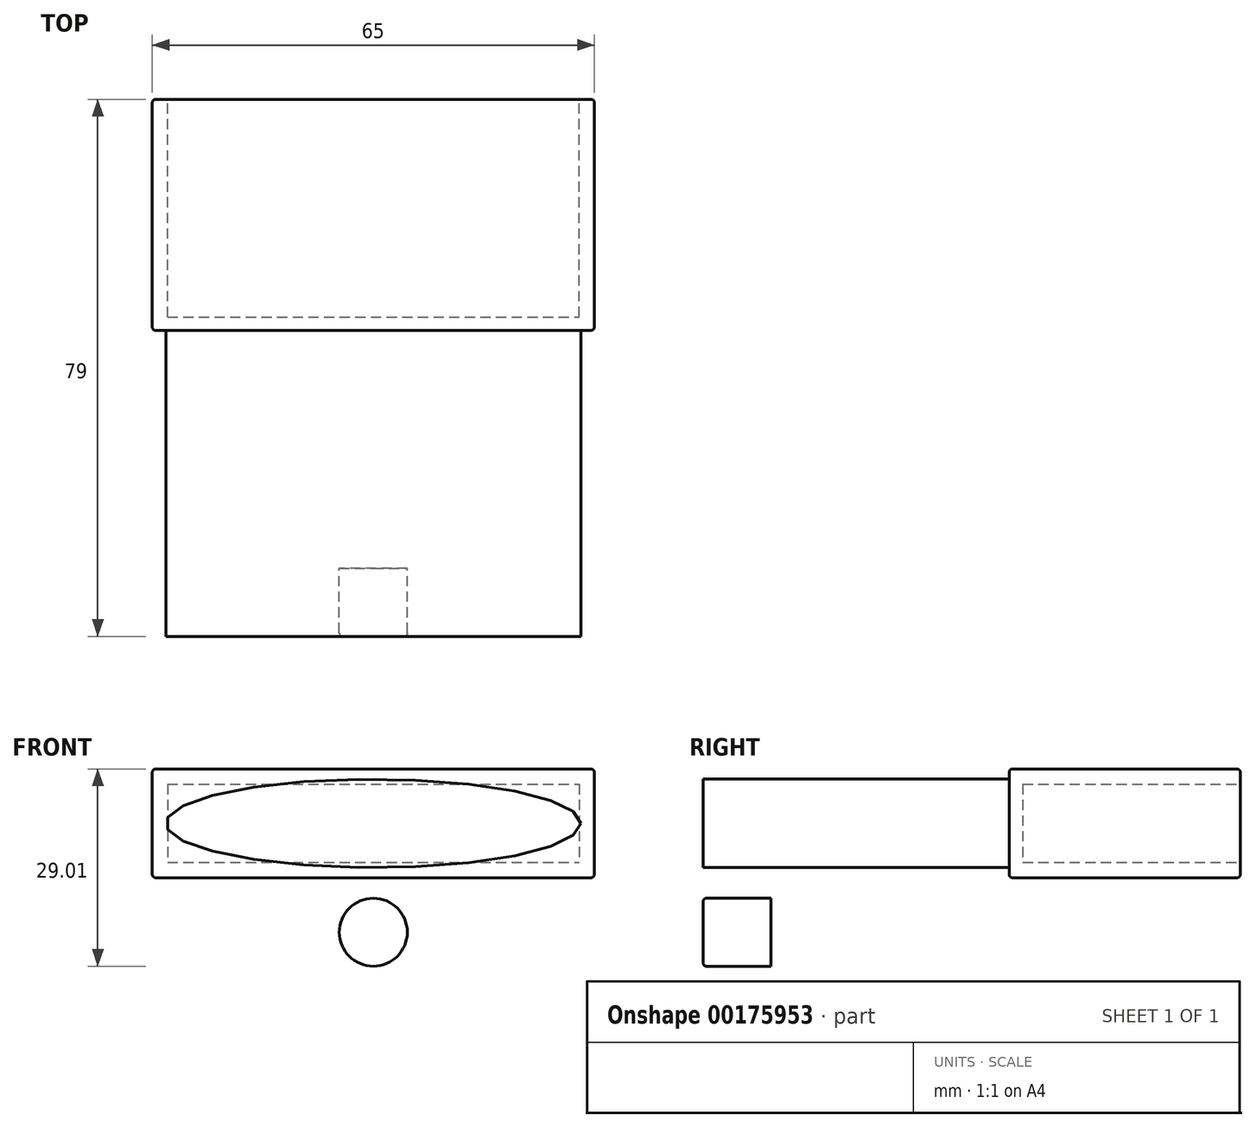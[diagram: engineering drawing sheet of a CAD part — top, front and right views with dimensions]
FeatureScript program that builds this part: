
annotation { "Feature Type Name" : "Feature", "Feature Type Description" : "" }
export const myFeature = defineFeature(function(context is Context, id is Id, definition is map)
    precondition{}
    {
        {
            var Q0;
            Q0=qCreatedBy(makeId("Front.planeOp"),FACE);
            var sketch = newSketch(context, id + "F0", { "sketchPlane" : qUnion([Q0])});
            skPoint(sketch, "E0.middle", {"position": v(0, 0) * mm});
            skLineSegment(sketch, "E1.bottom", {"start": v(32.5, 8) * mm, "end": v(-32.5, 8) * mm});
            skLineSegment(sketch, "E1.top", {"start": v(32.5, -8) * mm, "end": v(-32.5, -8) * mm});
            skLineSegment(sketch, "E1.left", {"start": v(32.5, 8) * mm, "end": v(32.5, -8) * mm});
            skLineSegment(sketch, "E1.right", {"start": v(-32.5, 8) * mm, "end": v(-32.5, -8) * mm});
            skSolve(sketch);
        }
        {
            var Q0;
            Q0=makeQuery(id+"F0.imprint","IMPRINT",FACE,{"disambiguationData":[TD([[makeQuery(id+"F0.imprint","IMPRINT",EDGE,{"derivedFrom":sQuery(id+"F0.wireOp",EDGE,"E1.bottom")}),1.0]])]});
            extrude(context, id + "F1", {"entities" : qUnion([Q0]), "depth" : 34 * mm});
        }
        {
            var Q0;
            Q0=makeQuery(id+"F1.opExtrude","CAP_FACE",FACE,{"disambiguationData":[OSD([sQuery(id+"F0.wireOp",EDGE,"E1.bottom"),sQuery(id+"F0.wireOp",EDGE,"E1.top"),sQuery(id+"F0.wireOp",EDGE,"E1.left"),sQuery(id+"F0.wireOp",EDGE,"E1.right")])],"isStart":false});
            var sketch = newSketch(context, id + "F2", { "sketchPlane" : qUnion([Q0])});
            skEllipse(sketch, "E2", {"center": v(0, 0) * mm, "majorRadius": 30.5 * mm, "minorRadius": 6.5 * mm, "majorAxis": v(1, 0)});
            skSolve(sketch);
        }
        {
            var Q0;
            Q0=makeQuery(id+"F1.opExtrude","CAP_FACE",FACE,{"disambiguationData":[OSD([sQuery(id+"F0.wireOp",EDGE,"E1.bottom"),sQuery(id+"F0.wireOp",EDGE,"E1.top"),sQuery(id+"F0.wireOp",EDGE,"E1.left"),sQuery(id+"F0.wireOp",EDGE,"E1.right")])],"isStart":true});
            var sketch = newSketch(context, id + "F3", { "sketchPlane" : qUnion([Q0])});
            skLineSegment(sketch, "E3.bottom", {"start": v(30.25, 5.75) * mm, "end": v(-30.25, 5.75) * mm});
            skLineSegment(sketch, "E3.top", {"start": v(30.25, -5.75) * mm, "end": v(-30.25, -5.75) * mm});
            skLineSegment(sketch, "E3.left", {"start": v(30.25, 5.75) * mm, "end": v(30.25, -5.75) * mm});
            skLineSegment(sketch, "E3.right", {"start": v(-30.25, 5.75) * mm, "end": v(-30.25, -5.75) * mm});
            skPoint(sketch, "E3.middle", {"position": v(0, 0) * mm});
            skSolve(sketch);
        }
        {
            var Q0;
            Q0=makeQuery(id+"F3.imprint","IMPRINT",FACE,{"disambiguationData":[TD([[makeQuery(id+"F3.imprint","IMPRINT",EDGE,{"derivedFrom":sQuery(id+"F3.wireOp",EDGE,"E3.bottom")}),1.0]])]});
            extrude(context, id + "F4", {"entities" : qUnion([Q0]), "operationType" : NewBodyOperationType.REMOVE, "oppositeDirection" : true, "depth" : 32 * mm});
        }
        {
            var Q0;
            Q0=makeQuery(id+"F2.imprint","IMPRINT",FACE,{"disambiguationData":[TD([[makeQuery(id+"F2.imprint","IMPRINT",EDGE,{"derivedFrom":sQuery(id+"F2.wireOp",EDGE,"E2")}),1.0]])]});
            extrude(context, id + "F5", {"entities" : qUnion([Q0]), "operationType" : NewBodyOperationType.ADD, "depth" : 35 * mm});
        }
        {
            var Q0;
            Q0=makeQuery(id+"F5.opExtrude","CAP_FACE",FACE,{"disambiguationData":[OSD([sQuery(id+"F2.wireOp",EDGE,"E2")])],"isStart":false});
            var sketch = newSketch(context, id + "F6", { "sketchPlane" : qUnion([Q0])});
            skEllipse(sketch, "E4", {"center": v(0, 0) * mm, "majorRadius": 50.5 * mm, "minorRadius": 25.5 * mm, "majorAxis": v(1, -0.06)});
            skSolve(sketch);
        }
        {
            var Q0;
            Q0=makeQuery(id+"F6.imprint","IMPRINT",FACE,{"disambiguationData":[TD([[makeQuery(id+"F6.imprint","IMPRINT",EDGE,{"derivedFrom":makeQuery(id+"F5.opExtrude","CAP_EDGE",EDGE,{"disambiguationData":[OSD([sQuery(id+"F2.wireOp",EDGE,"E2")])],"isStart":false})}),1.0]])]});
            var Q1;
            Q1=makeQuery(id+"F6.imprint","IMPRINT",FACE,{"disambiguationData":[TD([[makeQuery(id+"F6.imprint","IMPRINT",EDGE,{"derivedFrom":sQuery(id+"F6.wireOp",EDGE,"E4")}),1.0]])]});
            extrude(context, id + "F7", {"entities" : qUnion([Q0, Q1]), "operationType" : NewBodyOperationType.ADD, "depth" : 10 * mm});
        }
        {
            var Q0;
            Q0=makeQuery(id+"F7.opExtrude","CAP_FACE",FACE,{"disambiguationData":[OSD([sQuery(id+"F6.wireOp",EDGE,"E4")])],"isStart":true});
            var sketch = newSketch(context, id + "F8", { "sketchPlane" : qUnion([Q0])});
            skCircle(sketch, "E5", {"center": v(40.39, 0) * mm, "radius": 5 * mm});
            skCircle(sketch, "E6", {"center": v(-40.39, 0) * mm, "radius": 5 * mm});
            skCircle(sketch, "E7", {"center": v(0, 16.01) * mm, "radius": 5 * mm});
            skCircle(sketch, "E8.MirrorC", {"center": v(0, -16.01) * mm, "radius": 5 * mm});
            skSolve(sketch);
        }
        {
            var Q0;
            Q0=makeQuery(id+"F8.imprint","IMPRINT",FACE,{"disambiguationData":[TD([[makeQuery(id+"F8.imprint","IMPRINT",EDGE,{"derivedFrom":sQuery(id+"F8.wireOp",EDGE,"E5")}),1.0]])]});
            var Q1;
            Q1=makeQuery(id+"F8.imprint","IMPRINT",FACE,{"disambiguationData":[TD([[makeQuery(id+"F8.imprint","IMPRINT",EDGE,{"derivedFrom":sQuery(id+"F8.wireOp",EDGE,"E7")}),1.0]])]});
            var Q2;
            Q2=makeQuery(id+"F8.imprint","IMPRINT",FACE,{"disambiguationData":[TD([[makeQuery(id+"F8.imprint","IMPRINT",EDGE,{"derivedFrom":sQuery(id+"F8.wireOp",EDGE,"E6")}),1.0]])]});
            var Q3;
            Q3=makeQuery(id+"F8.imprint","IMPRINT",FACE,{"disambiguationData":[TD([[makeQuery(id+"F8.imprint","IMPRINT",EDGE,{"derivedFrom":sQuery(id+"F8.wireOp",EDGE,"E8.MirrorC")}),-1.0]])]});
            extrude(context, id + "F9", {"entities" : qUnion([Q0, Q1, Q2, Q3]), "operationType" : NewBodyOperationType.REMOVE, "endBound" : BoundingType.THROUGH_ALL, "oppositeDirection" : true, "depth" : 25 * mm});
        }
        {
            var Q0;
            Q0=makeQuery(id+"F1.opExtrude","CAP_EDGE",EDGE,{"disambiguationData":[OSD([sQuery(id+"F0.wireOp",EDGE,"E1.bottom")])],"isStart":true});
            var Q1;
            Q1=makeQuery(id+"F4.boolean.opBoolean","COPY",EDGE,{"derivedFrom":makeQuery(id+"F4.opExtrude","CAP_EDGE",EDGE,{"disambiguationData":[OSD([sQuery(id+"F3.wireOp",EDGE,"E3.bottom")])],"isStart":true})});
            var Q2;
            Q2=makeQuery(id+"F4.boolean.opBoolean","COPY",EDGE,{"derivedFrom":makeQuery(id+"F4.opExtrude","CAP_EDGE",EDGE,{"disambiguationData":[OSD([sQuery(id+"F3.wireOp",EDGE,"E3.right")])],"isStart":true})});
            var Q3;
            Q3=makeQuery(id+"F4.boolean.opBoolean","COPY",EDGE,{"derivedFrom":makeQuery(id+"F4.opExtrude","CAP_EDGE",EDGE,{"disambiguationData":[OSD([sQuery(id+"F3.wireOp",EDGE,"E3.top")])],"isStart":true})});
            var Q4;
            Q4=makeQuery(id+"F1.opExtrude","CAP_EDGE",EDGE,{"disambiguationData":[OSD([sQuery(id+"F0.wireOp",EDGE,"E1.left")])],"isStart":true});
            var Q5;
            Q5=makeQuery(id+"F1.opExtrude","CAP_EDGE",EDGE,{"disambiguationData":[OSD([sQuery(id+"F0.wireOp",EDGE,"E1.top")])],"isStart":true});
            var Q6;
            Q6=makeQuery(id+"F1.opExtrude","CAP_EDGE",EDGE,{"disambiguationData":[OSD([sQuery(id+"F0.wireOp",EDGE,"E1.right")])],"isStart":true});
            var Q7;
            Q7=makeQuery(id+"F4.boolean.opBoolean","COPY",EDGE,{"derivedFrom":makeQuery(id+"F4.opExtrude","CAP_EDGE",EDGE,{"disambiguationData":[OSD([sQuery(id+"F3.wireOp",EDGE,"E3.left")])],"isStart":true})});
            var Q8;
            Q8=makeQuery(id+"F1.opExtrude","SWEPT_EDGE",EDGE,{"disambiguationData":[OSD([sQuery(id+"F0.wireOp",EDGE,"E1.bottom"),sQuery(id+"F0.wireOp",EDGE,"E1.right")])]});
            var Q9;
            Q9=makeQuery(id+"F1.opExtrude","SWEPT_EDGE",EDGE,{"disambiguationData":[OSD([sQuery(id+"F0.wireOp",EDGE,"E1.top"),sQuery(id+"F0.wireOp",EDGE,"E1.right")])]});
            var Q10;
            Q10=makeQuery(id+"F1.opExtrude","CAP_EDGE",EDGE,{"disambiguationData":[OSD([sQuery(id+"F0.wireOp",EDGE,"E1.right")])],"isStart":false});
            var Q11;
            Q11=makeQuery(id+"F1.opExtrude","CAP_EDGE",EDGE,{"disambiguationData":[OSD([sQuery(id+"F0.wireOp",EDGE,"E1.bottom")])],"isStart":false});
            var Q12;
            Q12=makeQuery(id+"F1.opExtrude","SWEPT_EDGE",EDGE,{"disambiguationData":[OSD([sQuery(id+"F0.wireOp",EDGE,"E1.bottom"),sQuery(id+"F0.wireOp",EDGE,"E1.left")])]});
            var Q13;
            Q13=makeQuery(id+"F1.opExtrude","SWEPT_EDGE",EDGE,{"disambiguationData":[OSD([sQuery(id+"F0.wireOp",EDGE,"E1.top"),sQuery(id+"F0.wireOp",EDGE,"E1.left")])]});
            var Q14;
            Q14=makeQuery(id+"F1.opExtrude","CAP_EDGE",EDGE,{"disambiguationData":[OSD([sQuery(id+"F0.wireOp",EDGE,"E1.left")])],"isStart":false});
            var Q15;
            Q15=makeQuery(id+"F1.opExtrude","CAP_EDGE",EDGE,{"disambiguationData":[OSD([sQuery(id+"F0.wireOp",EDGE,"E1.top")])],"isStart":false});
            var Q16;
            Q16=makeQuery(id+"F7.opExtrude","CAP_EDGE",EDGE,{"disambiguationData":[OSD([sQuery(id+"F6.wireOp",EDGE,"E4")])],"isStart":true});
            var Q17;
            Q17=makeQuery(id+"F7.opExtrude","CAP_EDGE",EDGE,{"disambiguationData":[OSD([sQuery(id+"F6.wireOp",EDGE,"E4")])],"isStart":false});
            var Q18;
            Q18=makeQuery(id+"F9.boolean.opBoolean","INTERSECT",EDGE,{"derivedFrom":[makeQuery(id+"F7.opExtrude","CAP_FACE",FACE,{"disambiguationData":[OSD([sQuery(id+"F6.wireOp",EDGE,"E4")])],"isStart":false}),makeQuery(id+"F9.opExtrude","SWEPT_FACE",FACE,{"disambiguationData":[OSD([sQuery(id+"F8.wireOp",EDGE,"E6")])]})]});
            var Q19;
            Q19=makeQuery(id+"F9.boolean.opBoolean","INTERSECT",EDGE,{"derivedFrom":[makeQuery(id+"F7.opExtrude","CAP_FACE",FACE,{"disambiguationData":[OSD([sQuery(id+"F6.wireOp",EDGE,"E4")])],"isStart":false}),makeQuery(id+"F9.opExtrude","SWEPT_FACE",FACE,{"disambiguationData":[OSD([sQuery(id+"F8.wireOp",EDGE,"E8.MirrorC")])]})]});
            var Q20;
            Q20=makeQuery(id+"F9.boolean.opBoolean","INTERSECT",EDGE,{"derivedFrom":[makeQuery(id+"F7.opExtrude","CAP_FACE",FACE,{"disambiguationData":[OSD([sQuery(id+"F6.wireOp",EDGE,"E4")])],"isStart":false}),makeQuery(id+"F9.opExtrude","SWEPT_FACE",FACE,{"disambiguationData":[OSD([sQuery(id+"F8.wireOp",EDGE,"E7")])]})]});
            var Q21;
            Q21=makeQuery(id+"F9.boolean.opBoolean","INTERSECT",EDGE,{"derivedFrom":[makeQuery(id+"F7.opExtrude","CAP_FACE",FACE,{"disambiguationData":[OSD([sQuery(id+"F6.wireOp",EDGE,"E4")])],"isStart":false}),makeQuery(id+"F9.opExtrude","SWEPT_FACE",FACE,{"disambiguationData":[OSD([sQuery(id+"F8.wireOp",EDGE,"E5")])]})]});
            var Q22;
            Q22=makeQuery(id+"F9.boolean.opBoolean","COPY",EDGE,{"derivedFrom":makeQuery(id+"F9.opExtrude","CAP_EDGE",EDGE,{"disambiguationData":[OSD([sQuery(id+"F8.wireOp",EDGE,"E6")])],"isStart":true})});
            var Q23;
            Q23=makeQuery(id+"F9.boolean.opBoolean","COPY",EDGE,{"derivedFrom":makeQuery(id+"F9.opExtrude","CAP_EDGE",EDGE,{"disambiguationData":[OSD([sQuery(id+"F8.wireOp",EDGE,"E7")])],"isStart":true})});
            var Q24;
            Q24=makeQuery(id+"F9.boolean.opBoolean","COPY",EDGE,{"derivedFrom":makeQuery(id+"F9.opExtrude","CAP_EDGE",EDGE,{"disambiguationData":[OSD([sQuery(id+"F8.wireOp",EDGE,"E8.MirrorC")])],"isStart":true})});
            var Q25;
            Q25=makeQuery(id+"F9.boolean.opBoolean","COPY",EDGE,{"derivedFrom":makeQuery(id+"F9.opExtrude","CAP_EDGE",EDGE,{"disambiguationData":[OSD([sQuery(id+"F8.wireOp",EDGE,"E5")])],"isStart":true})});
            fillet(context, id + "F10", {"entities" : qUnion([Q0, Q1, Q2, Q3, Q4, Q5, Q6, Q7, Q8, Q9, Q10, Q11, Q12, Q13, Q14, Q15, Q16, Q17, Q18, Q19, Q20, Q21, Q22, Q23, Q24, Q25]), "radius" : .5 * mm, "tangentPropagation" : true, "allowEdgeOverflow" : false});
        }
    });
